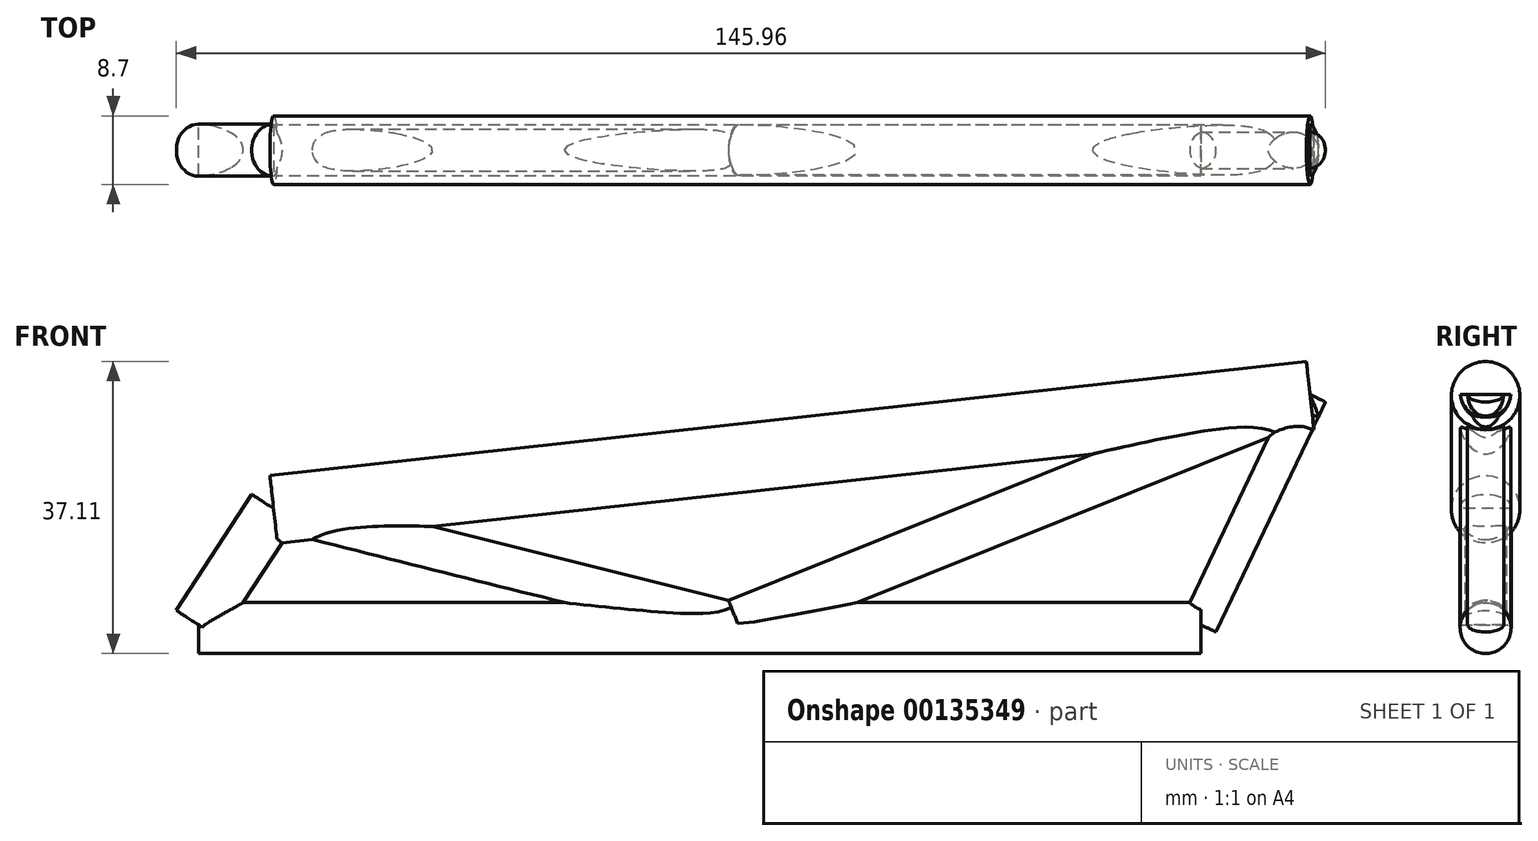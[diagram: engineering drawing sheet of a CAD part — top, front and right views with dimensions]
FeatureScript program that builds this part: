
annotation { "Feature Type Name" : "Feature", "Feature Type Description" : "" }
export const myFeature = defineFeature(function(context is Context, id is Id, definition is map)
    precondition{}
    {
        {
            var Q0;
            Q0=qCreatedBy(makeId("Front.planeOp"),FACE);
            var sketch = newSketch(context, id + "F0", { "sketchPlane" : qUnion([Q0])});
            skLineSegment(sketch, "E0", {"start": v(-68.58, -9.98) * mm, "end": v(58.74, -9.98) * mm});
            skLineSegment(sketch, "E1", {"start": v(58.74, -9.98) * mm, "end": v(72.63, 19.24) * mm});
            skLineSegment(sketch, "E2", {"start": v(72.63, 19.24) * mm, "end": v(-59.03, 4.77) * mm});
            skLineSegment(sketch, "E3", {"start": v(-59.03, 4.77) * mm, "end": v(-68.58, -9.98) * mm});
            skLineSegment(sketch, "E4", {"start": v(-59.03, 4.77) * mm, "end": v(0, -9.98) * mm});
            skLineSegment(sketch, "E5", {"start": v(0, -9.98) * mm, "end": v(72.63, 19.24) * mm});
            skSolve(sketch);
        }
        {
            var Q0;
            Q0=sQuery(id+"F0.wireOp",VERTEX,"E4.start");
            var Q1;
            Q1=sQuery(id+"F0.wireOp",EDGE,"E2");
            cPlane(context, id + "F1", {"entities" : qUnion([Q0, Q1]), "cplaneType" : CPlaneType.CURVE_POINT, "offset" : 25.4 * mm, "width" : 152.4 * mm, "height" : 152.4 * mm});
        }
        {
            var Q0;
            Q0=qCreatedBy(id+"F1.planeOp",FACE);
            var sketch = newSketch(context, id + "F2", { "sketchPlane" : qUnion([Q0])});
            skCircle(sketch, "E6", {"center": v(0, 11.09) * mm, "radius": 4.35 * mm});
            skSolve(sketch);
        }
        {
            var Q0;
            Q0=makeQuery(id+"F2.imprint","IMPRINT",FACE,{"disambiguationData":[TD([[makeQuery(id+"F2.imprint","IMPRINT",EDGE,{"derivedFrom":sQuery(id+"F2.wireOp",EDGE,"E6")}),1.0]])]});
            var Q1;
            Q1=sQuery(id+"F0.wireOp",EDGE,"E2");
            sweep(context, id + "F3", {"profiles" : qUnion([Q0]), "path" : qUnion([Q1])});
        }
        {
            var Q0;
            Q0=sQuery(id+"F0.wireOp",VERTEX,"E4.start");
            var Q1;
            Q1=sQuery(id+"F0.wireOp",EDGE,"E4");
            cPlane(context, id + "F4", {"entities" : qUnion([Q0, Q1]), "cplaneType" : CPlaneType.CURVE_POINT, "offset" : 25.4 * mm, "width" : 152.4 * mm, "height" : 152.4 * mm});
        }
        {
            var Q0;
            Q0=qCreatedBy(id+"F4.planeOp",FACE);
            var sketch = newSketch(context, id + "F5", { "sketchPlane" : qUnion([Q0])});
            skCircle(sketch, "E7", {"center": v(0, -9.65) * mm, "radius": 2.66 * mm});
            skSolve(sketch);
        }
        {
            var Q0;
            Q0=makeQuery(id+"F5.imprint","IMPRINT",FACE,{"disambiguationData":[TD([[makeQuery(id+"F5.imprint","IMPRINT",EDGE,{"derivedFrom":sQuery(id+"F5.wireOp",EDGE,"E7")}),1.0]])]});
            var Q1;
            Q1=sQuery(id+"F0.wireOp",EDGE,"E4");
            sweep(context, id + "F6", {"operationType" : NewBodyOperationType.ADD, "profiles" : qUnion([Q0]), "path" : qUnion([Q1])});
        }
        {
            var Q0;
            Q0=sQuery(id+"F0.wireOp",VERTEX,"E3.end");
            var Q1;
            Q1=sQuery(id+"F0.wireOp",EDGE,"E0");
            cPlane(context, id + "F7", {"entities" : qUnion([Q0, Q1]), "cplaneType" : CPlaneType.CURVE_POINT, "offset" : 25.4 * mm, "width" : 152.4 * mm, "height" : 152.4 * mm});
        }
        {
            var Q0;
            Q0=qCreatedBy(id+"F7.planeOp",FACE);
            var sketch = newSketch(context, id + "F8", { "sketchPlane" : qUnion([Q0])});
            skCircle(sketch, "E8", {"center": v(0, -10.42) * mm, "radius": 3.24 * mm});
            skSolve(sketch);
        }
        {
            var Q0;
            Q0=makeQuery(id+"F8.imprint","IMPRINT",FACE,{"disambiguationData":[TD([[makeQuery(id+"F8.imprint","IMPRINT",EDGE,{"derivedFrom":sQuery(id+"F8.wireOp",EDGE,"E8")}),1.0]])]});
            var Q1;
            Q1=sQuery(id+"F0.wireOp",EDGE,"E0");
            sweep(context, id + "F9", {"operationType" : NewBodyOperationType.ADD, "profiles" : qUnion([Q0]), "path" : qUnion([Q1])});
        }
        {
            var Q0;
            Q0=sQuery(id+"F0.wireOp",VERTEX,"E3.end");
            var Q1;
            Q1=sQuery(id+"F0.wireOp",EDGE,"E3");
            cPlane(context, id + "F10", {"entities" : qUnion([Q0, Q1]), "cplaneType" : CPlaneType.CURVE_POINT, "offset" : 25.4 * mm, "width" : 152.4 * mm, "height" : 152.4 * mm});
        }
        {
            var Q0;
            Q0=qCreatedBy(id+"F10.planeOp",FACE);
            var sketch = newSketch(context, id + "F11", { "sketchPlane" : qUnion([Q0])});
            skCircle(sketch, "E9", {"center": v(-52.2, 0) * mm, "radius": 3.3 * mm});
            skSolve(sketch);
        }
        {
            var Q0;
            Q0=makeQuery(id+"F11.imprint","IMPRINT",FACE,{"disambiguationData":[TD([[makeQuery(id+"F11.imprint","IMPRINT",EDGE,{"derivedFrom":sQuery(id+"F11.wireOp",EDGE,"E9")}),1.0]])]});
            var Q1;
            Q1=sQuery(id+"F0.wireOp",EDGE,"E3");
            sweep(context, id + "F12", {"operationType" : NewBodyOperationType.ADD, "profiles" : qUnion([Q0]), "path" : qUnion([Q1])});
        }
        {
            var Q0;
            Q0=sQuery(id+"F0.wireOp",VERTEX,"E5.end");
            var Q1;
            Q1=sQuery(id+"F0.wireOp",EDGE,"E5");
            cPlane(context, id + "F13", {"entities" : qUnion([Q0, Q1]), "cplaneType" : CPlaneType.CURVE_POINT, "offset" : 25.4 * mm, "width" : 152.4 * mm, "height" : 152.4 * mm});
        }
        {
            var Q0;
            Q0=qCreatedBy(id+"F13.planeOp",FACE);
            var sketch = newSketch(context, id + "F14", { "sketchPlane" : qUnion([Q0])});
            skCircle(sketch, "E10", {"center": v(0, -9.11) * mm, "radius": 3.18 * mm});
            skSolve(sketch);
        }
        {
            var Q0;
            Q0=makeQuery(id+"F14.imprint","IMPRINT",FACE,{"disambiguationData":[TD([[makeQuery(id+"F14.imprint","IMPRINT",EDGE,{"derivedFrom":sQuery(id+"F14.wireOp",EDGE,"E10")}),1.0]])]});
            var Q1;
            Q1=sQuery(id+"F0.wireOp",EDGE,"E5");
            sweep(context, id + "F15", {"operationType" : NewBodyOperationType.ADD, "profiles" : qUnion([Q0]), "path" : qUnion([Q1])});
        }
        {
            var Q0;
            Q0=sQuery(id+"F0.wireOp",VERTEX,"E1.start");
            var Q1;
            Q1=sQuery(id+"F0.wireOp",EDGE,"E1");
            cPlane(context, id + "F16", {"entities" : qUnion([Q0, Q1]), "cplaneType" : CPlaneType.CURVE_POINT, "offset" : 25.4 * mm, "width" : 152.4 * mm, "height" : 152.4 * mm});
        }
        {
            var Q0;
            Q0=qCreatedBy(id+"F16.planeOp",FACE);
            var sketch = newSketch(context, id + "F17", { "sketchPlane" : qUnion([Q0])});
            skCircle(sketch, "E11", {"center": v(57.19, 0) * mm, "radius": 2.31 * mm});
            skSolve(sketch);
        }
        {
            var Q0;
            Q0=makeQuery(id+"F17.imprint","IMPRINT",FACE,{"disambiguationData":[TD([[makeQuery(id+"F17.imprint","IMPRINT",EDGE,{"derivedFrom":sQuery(id+"F17.wireOp",EDGE,"E11")}),1.0]])]});
            var Q1;
            Q1=sQuery(id+"F0.wireOp",EDGE,"E1");
            sweep(context, id + "F18", {"operationType" : NewBodyOperationType.ADD, "profiles" : qUnion([Q0]), "path" : qUnion([Q1])});
        }
    });
